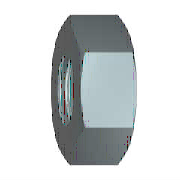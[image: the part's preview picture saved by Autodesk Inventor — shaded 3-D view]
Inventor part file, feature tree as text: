
AUTODESK INVENTOR PART (.ipt)
format: ipt  version: 2022 (Build 260153000, 153)  size: 163,840 bytes
history: native  units: mm (DEFAULTED — no unit token found)
features: sketch x3, chamfer x1, hole x1, other x1, plane x1
ambient origin geometry x7: Origin, YZ Plane, XZ Plane, X Axis, Y Axis, Z Axis, Center Point
bodies: Solid1 (feature_tree), Body (feature_tree)
feature tree (7):
  chamfer  "Chamfer1"  Angle=30.0deg  [1 undecoded]
  hole  "Thread"  [1 undecoded]
  other  "Work Axis1"
  plane  "Work Plane1"
  sketch  "Sketch1"  dims[d0=8.082904mm]
  sketch  "Sketch2"  dims[d1=3.2mm]
  sketch  "Sketch3"  dims[d2=0.0mm d3=30.0deg d4=30.0deg d5=5.9mm d6=5.9mm d7=90.0deg d25=3.242mm d26=6.0mm d27=4.0mm d28=2.0mm d29=14.3117mm d30=8.0mm d31=20.594885mm d8=0.378886mm d9=30.0deg d10=0.378886mm d11=30.0deg d13=0.0mm d14=0.0mm d39=0.0mm d40=0.378886mm d41=0.378886mm d42=0.0mm]
note: 2 required parameter values undecoded (feature->parameter linkage not recoverable at this tier; creation-order binding heuristic only, values carry confidence <= 0.55)
